# Revit family: 820-00-024 DN65-100
name_source: partatom
category: Pipe Accessories
units: mm (PartAtom-declared; Revit-internal decimal feet)

## family parameters
Always vertical = Yes
Cut with Voids When Loaded = No
Part Type = Valve - Breaks Into
Round Connector Dimension = Use Diameter
Shared = No
Work Plane-Based = No

## types (3) — shared parameters
1 = 1 mm  [stored 0.00328084 ft]
90 = 90 mm
Body_wallthickness = 10 mm  [stored 0.0328084 ft]
DN100_PN10/16 = 820-0100-00-521L0160002
DN65_PN10/16 = 820-0065-00-521L0160002
DN80_PN10/16 = 820-0080-00-521L0160002
Description_ = AVK CENTRIC BUTTERFLY VALVE WAFER TYPE, PN10/16
F = 11 mm  [stored 0.0360892 ft]
F2 = 12 mm  [stored 0.0393701 ft]
FL_T = 15 mm  [stored 0.0492126 ft]
Hole_dia = 19 mm  [stored 0.062336 ft]
Lug_D = 13 mm  [stored 0.0426509 ft]
Search_table = 820-00-024 DN65-100
URL product pages = https://www.avkvalves.com
fillet = 20 mm  [stored 0.0656168 ft]
zero-valued in all types: Default Elevation

## per-type parameters (varying)
| type | Actuator_Dia | Bore | DN | EPDM | EPDM_R | FL_R | Flange_thickness | H2 | Hole_L | Hole_L1 | ID | L | L-2 | L2 | LUG_T | L_ref | L_ref_2 | L_ref_3 | PCD | W2_ref | Wafer_dim | Wafer_dim1 | disk |
| DN65_PN10/16 | 65 mm  [stored 0.213255 ft] | 33 mm  [stored 0.108268 ft] | 65 mm  [stored 0.213255 ft] | 32 mm  [stored 0.104987 ft] | 43 mm  [stored 0.141076 ft] | 43 mm  [stored 0.141076 ft] | 7 mm  [stored 0.0229659 ft] | 82 mm | 35 mm  [stored 0.114829 ft] | 49 mm  [stored 0.160761 ft] | 33 mm  [stored 0.108268 ft] | 46 mm  [stored 0.150919 ft] | 44 mm  [stored 0.144357 ft] | 69 mm  [stored 0.226378 ft] | 22 mm  [stored 0.0721785 ft] | 30 mm  [stored 0.0984252 ft] | 60 mm  [stored 0.19685 ft] | 25 mm  [stored 0.082021 ft] | 73 mm | 150 mm | 41 mm | 66 mm  [stored 0.216535 ft] | 17 mm  [stored 0.0557743 ft] |
| DN80_PN10/16 | 65 mm  [stored 0.213255 ft] | 40 mm  [stored 0.131234 ft] | 80 mm | 39 mm  [stored 0.127953 ft] | 50 mm  [stored 0.164042 ft] | 50 mm  [stored 0.164042 ft] | 8 mm  [stored 0.0262467 ft] | 92 mm | 36 mm  [stored 0.11811 ft] | 55 mm  [stored 0.180446 ft] | 40 mm  [stored 0.131234 ft] | 46 mm  [stored 0.150919 ft] | 44 mm  [stored 0.144357 ft] | 71 mm  [stored 0.23294 ft] | 22 mm  [stored 0.0721785 ft] | 28 mm  [stored 0.0918635 ft] | 56 mm  [stored 0.183727 ft] | 23 mm  [stored 0.0754593 ft] | 80 mm | 160 mm | 43 mm  [stored 0.141076 ft] | 74 mm | 17 mm  [stored 0.0557743 ft] |
| DN100_PN10/16 | 90 mm | 50 mm  [stored 0.164042 ft] | 100 mm | 49 mm  [stored 0.160761 ft] | 60 mm  [stored 0.19685 ft] | 60 mm  [stored 0.19685 ft] | 8 mm  [stored 0.0262467 ft] | 110 mm | 41 mm | 66 mm  [stored 0.216535 ft] | 50 mm  [stored 0.164042 ft] | 52 mm | 50 mm  [stored 0.164042 ft] | 81 mm | 25 mm  [stored 0.082021 ft] | 34 mm | 68 mm  [stored 0.223097 ft] | 28 mm  [stored 0.0918635 ft] | 90 mm | 180 mm | 49 mm  [stored 0.160761 ft] | 88 mm | 19 mm  [stored 0.062336 ft] |

note: [stored X ft] marks values corroborated as IEEE doubles in the binary element streams (Revit-internal decimal feet)

## geometry (parser evidence)
native form markers: Sweep x4
no freeform markers — native parametric forms only
